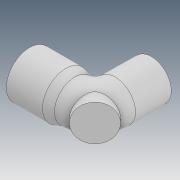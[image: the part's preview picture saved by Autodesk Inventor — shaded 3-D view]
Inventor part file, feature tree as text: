
AUTODESK INVENTOR PART (.ipt)
format: ipt  version: 2020 (Build 240168000, 168)  size: 193,536 bytes
history: native  units: mm
features: sketch x4, revolve x3, plane x2, extrude x1, projected_geometry x1
ambient origin geometry x8: Origin, YZ Plane, XZ Plane, XY Plane, X Axis, Y Axis, Z Axis, Center Point
bodies: Solid1 (feature_tree)
feature tree (11):
  revolve  "Revolution1"  [1 undecoded]
  revolve  "Revolution2"  [1 undecoded]
  revolve  "Revolution3"  [1 undecoded]
  plane  "Work Plane2"
  extrude  "Extrusion1"  Depth=10.0mm
  sketch  "Sketch1"  dims[d0=11.2mm d1=20.0mm]
  sketch  "Sketch2"  dims[d2=11.0mm d3=1.6mm]
  sketch  "Sketch3"  dims[d4=0.0mm d5=5.0mm]
  plane  "Work Plane1"
  sketch  "Sketch4"  dims[d6=11.2mm d7=1.8mm d8=90.0deg d9=11.2mm d10=90.0deg d11=20.0mm d12=11.0mm d13=90.0deg d14=-7.853982mm d15=33.0mm d16=20.0mm d17=10.0mm d18=0.0mm]
  projected_geometry  "Projected Loop1"
note: 3 required parameter values undecoded (feature->parameter linkage not recoverable at this tier; creation-order binding heuristic only, values carry confidence <= 0.55)
